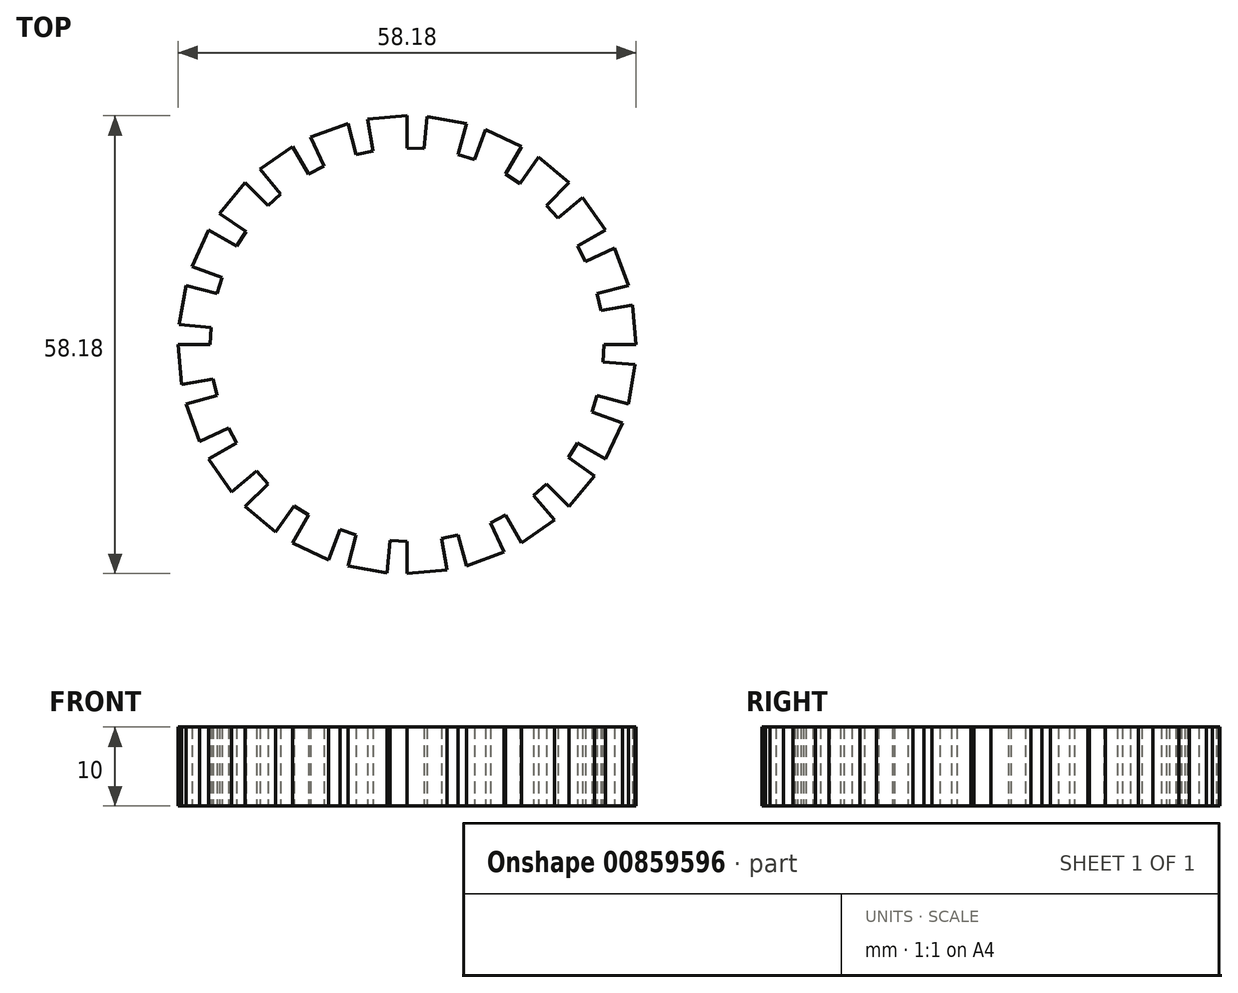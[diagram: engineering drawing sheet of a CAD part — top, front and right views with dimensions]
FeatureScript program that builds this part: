
annotation { "Feature Type Name" : "Feature", "Feature Type Description" : "" }
export const myFeature = defineFeature(function(context is Context, id is Id, definition is map)
    precondition{}
    {
        {
            var Q0;
            Q0=qCreatedBy(makeId("Top.planeOp"),FACE);
            var sketch = newSketch(context, id + "F0", { "sketchPlane" : qUnion([Q0])});
            skCircle(sketch, "E0", {"center": v(0, 0) * mm, "radius": 25 * mm, "construction": true});
            skLineSegment(sketch, "E1", {"start": v(0, 25) * mm, "end": v(0, 29.09) * mm});
            skCircle(sketch, "E2", {"center": v(0, 0) * mm, "radius": 29.09 * mm, "construction": true});
            skLineSegment(sketch, "E3", {"start": v(0, 0) * mm, "end": v(-5.05, 28.65) * mm, "construction": true});
            skLineSegment(sketch, "E4", {"start": v(0, 29.09) * mm, "end": v(-5.05, 28.65) * mm});
            skLineSegment(sketch, "E5", {"start": v(0, 0) * mm, "end": v(-7.53, 28.1) * mm, "construction": true});
            skLineSegment(sketch, "E6", {"start": v(-5.05, 28.65) * mm, "end": v(-4.34, 24.62) * mm});
            skLineSegment(sketch, "E7", {"start": v(-4.34, 24.62) * mm, "end": v(-6.47, 24.15) * mm});
            skLineSegment(sketch, "E8.1.0", {"start": v(-6.47, 24.15) * mm, "end": v(-7.53, 28.1) * mm});
            skLineSegment(sketch, "E8.1.1", {"start": v(-12.3, 26.36) * mm, "end": v(-10.57, 22.66) * mm});
            skLineSegment(sketch, "E8.1.2", {"start": v(-10.57, 22.66) * mm, "end": v(-12.5, 21.65) * mm});
            skLineSegment(sketch, "E8.1.3", {"start": v(-7.53, 28.1) * mm, "end": v(-12.3, 26.36) * mm});
            skLineSegment(sketch, "E8.2.0", {"start": v(-12.5, 21.65) * mm, "end": v(-14.54, 25.2) * mm});
            skLineSegment(sketch, "E8.2.1", {"start": v(-18.7, 22.28) * mm, "end": v(-16.07, 19.15) * mm});
            skLineSegment(sketch, "E8.2.2", {"start": v(-16.07, 19.15) * mm, "end": v(-17.68, 17.68) * mm});
            skLineSegment(sketch, "E8.2.3", {"start": v(-14.54, 25.2) * mm, "end": v(-18.7, 22.28) * mm});
            skLineSegment(sketch, "E8.3.0", {"start": v(-17.68, 17.68) * mm, "end": v(-20.57, 20.57) * mm});
            skLineSegment(sketch, "E8.3.1", {"start": v(-23.83, 16.68) * mm, "end": v(-20.48, 14.34) * mm});
            skLineSegment(sketch, "E8.3.2", {"start": v(-20.48, 14.34) * mm, "end": v(-21.65, 12.5) * mm});
            skLineSegment(sketch, "E8.3.3", {"start": v(-20.57, 20.57) * mm, "end": v(-23.83, 16.68) * mm});
            skLineSegment(sketch, "E8.4.0", {"start": v(-21.65, 12.5) * mm, "end": v(-25.2, 14.54) * mm});
            skLineSegment(sketch, "E8.4.1", {"start": v(-27.33, 9.95) * mm, "end": v(-23.5, 8.55) * mm});
            skLineSegment(sketch, "E8.4.2", {"start": v(-23.5, 8.55) * mm, "end": v(-24.15, 6.47) * mm});
            skLineSegment(sketch, "E8.4.3", {"start": v(-25.2, 14.54) * mm, "end": v(-27.33, 9.95) * mm});
            skLineSegment(sketch, "E8.5.0", {"start": v(-24.15, 6.47) * mm, "end": v(-28.1, 7.53) * mm});
            skLineSegment(sketch, "E8.5.1", {"start": v(-28.98, 2.54) * mm, "end": v(-24.9, 2.18) * mm});
            skLineSegment(sketch, "E8.5.2", {"start": v(-24.9, 2.18) * mm, "end": v(-25, 0) * mm});
            skLineSegment(sketch, "E8.5.3", {"start": v(-28.1, 7.53) * mm, "end": v(-28.98, 2.54) * mm});
            skLineSegment(sketch, "E8.6.0", {"start": v(-25, 0) * mm, "end": v(-29.09, 0) * mm});
            skLineSegment(sketch, "E8.6.1", {"start": v(-28.65, -5.05) * mm, "end": v(-24.62, -4.34) * mm});
            skLineSegment(sketch, "E8.6.2", {"start": v(-24.62, -4.34) * mm, "end": v(-24.15, -6.47) * mm});
            skLineSegment(sketch, "E8.6.3", {"start": v(-29.09, 0) * mm, "end": v(-28.65, -5.05) * mm});
            skLineSegment(sketch, "E8.7.0", {"start": v(-24.15, -6.47) * mm, "end": v(-28.1, -7.53) * mm});
            skLineSegment(sketch, "E8.7.1", {"start": v(-26.36, -12.3) * mm, "end": v(-22.66, -10.57) * mm});
            skLineSegment(sketch, "E8.7.2", {"start": v(-22.66, -10.57) * mm, "end": v(-21.65, -12.5) * mm});
            skLineSegment(sketch, "E8.7.3", {"start": v(-28.1, -7.53) * mm, "end": v(-26.36, -12.3) * mm});
            skLineSegment(sketch, "E8.8.0", {"start": v(-21.65, -12.5) * mm, "end": v(-25.2, -14.54) * mm});
            skLineSegment(sketch, "E8.8.1", {"start": v(-22.28, -18.7) * mm, "end": v(-19.15, -16.07) * mm});
            skLineSegment(sketch, "E8.8.2", {"start": v(-19.15, -16.07) * mm, "end": v(-17.68, -17.68) * mm});
            skLineSegment(sketch, "E8.8.3", {"start": v(-25.2, -14.54) * mm, "end": v(-22.28, -18.7) * mm});
            skLineSegment(sketch, "E8.9.0", {"start": v(-17.68, -17.68) * mm, "end": v(-20.57, -20.57) * mm});
            skLineSegment(sketch, "E8.9.1", {"start": v(-16.68, -23.83) * mm, "end": v(-14.34, -20.48) * mm});
            skLineSegment(sketch, "E8.9.2", {"start": v(-14.34, -20.48) * mm, "end": v(-12.5, -21.65) * mm});
            skLineSegment(sketch, "E8.9.3", {"start": v(-20.57, -20.57) * mm, "end": v(-16.68, -23.83) * mm});
            skLineSegment(sketch, "E8.10.0", {"start": v(-12.5, -21.65) * mm, "end": v(-14.54, -25.2) * mm});
            skLineSegment(sketch, "E8.10.1", {"start": v(-9.95, -27.33) * mm, "end": v(-8.55, -23.5) * mm});
            skLineSegment(sketch, "E8.10.2", {"start": v(-8.55, -23.5) * mm, "end": v(-6.47, -24.15) * mm});
            skLineSegment(sketch, "E8.10.3", {"start": v(-14.54, -25.2) * mm, "end": v(-9.95, -27.33) * mm});
            skLineSegment(sketch, "E8.11.0", {"start": v(-6.47, -24.15) * mm, "end": v(-7.53, -28.1) * mm});
            skLineSegment(sketch, "E8.11.1", {"start": v(-2.54, -28.98) * mm, "end": v(-2.18, -24.9) * mm});
            skLineSegment(sketch, "E8.11.2", {"start": v(-2.18, -24.9) * mm, "end": v(0, -25) * mm});
            skLineSegment(sketch, "E8.11.3", {"start": v(-7.53, -28.1) * mm, "end": v(-2.54, -28.98) * mm});
            skLineSegment(sketch, "E8.12.0", {"start": v(0, -25) * mm, "end": v(0, -29.09) * mm});
            skLineSegment(sketch, "E8.12.1", {"start": v(5.05, -28.65) * mm, "end": v(4.34, -24.62) * mm});
            skLineSegment(sketch, "E8.12.2", {"start": v(4.34, -24.62) * mm, "end": v(6.47, -24.15) * mm});
            skLineSegment(sketch, "E8.12.3", {"start": v(0, -29.09) * mm, "end": v(5.05, -28.65) * mm});
            skLineSegment(sketch, "E8.13.0", {"start": v(6.47, -24.15) * mm, "end": v(7.53, -28.1) * mm});
            skLineSegment(sketch, "E8.13.1", {"start": v(12.3, -26.36) * mm, "end": v(10.57, -22.66) * mm});
            skLineSegment(sketch, "E8.13.2", {"start": v(10.57, -22.66) * mm, "end": v(12.5, -21.65) * mm});
            skLineSegment(sketch, "E8.13.3", {"start": v(7.53, -28.1) * mm, "end": v(12.3, -26.36) * mm});
            skLineSegment(sketch, "E8.14.0", {"start": v(12.5, -21.65) * mm, "end": v(14.54, -25.2) * mm});
            skLineSegment(sketch, "E8.14.1", {"start": v(18.7, -22.28) * mm, "end": v(16.07, -19.15) * mm});
            skLineSegment(sketch, "E8.14.2", {"start": v(16.07, -19.15) * mm, "end": v(17.68, -17.68) * mm});
            skLineSegment(sketch, "E8.14.3", {"start": v(14.54, -25.2) * mm, "end": v(18.7, -22.28) * mm});
            skLineSegment(sketch, "E8.15.0", {"start": v(17.68, -17.68) * mm, "end": v(20.57, -20.57) * mm});
            skLineSegment(sketch, "E8.15.1", {"start": v(23.83, -16.68) * mm, "end": v(20.48, -14.34) * mm});
            skLineSegment(sketch, "E8.15.2", {"start": v(20.48, -14.34) * mm, "end": v(21.65, -12.5) * mm});
            skLineSegment(sketch, "E8.15.3", {"start": v(20.57, -20.57) * mm, "end": v(23.83, -16.68) * mm});
            skLineSegment(sketch, "E8.16.0", {"start": v(21.65, -12.5) * mm, "end": v(25.2, -14.54) * mm});
            skLineSegment(sketch, "E8.16.1", {"start": v(27.33, -9.95) * mm, "end": v(23.5, -8.55) * mm});
            skLineSegment(sketch, "E8.16.2", {"start": v(23.5, -8.55) * mm, "end": v(24.15, -6.47) * mm});
            skLineSegment(sketch, "E8.16.3", {"start": v(25.2, -14.54) * mm, "end": v(27.33, -9.95) * mm});
            skLineSegment(sketch, "E8.17.0", {"start": v(24.15, -6.47) * mm, "end": v(28.1, -7.53) * mm});
            skLineSegment(sketch, "E8.17.1", {"start": v(28.98, -2.54) * mm, "end": v(24.9, -2.18) * mm});
            skLineSegment(sketch, "E8.17.2", {"start": v(24.9, -2.18) * mm, "end": v(25, 0) * mm});
            skLineSegment(sketch, "E8.17.3", {"start": v(28.1, -7.53) * mm, "end": v(28.98, -2.54) * mm});
            skLineSegment(sketch, "E9.1.18.0", {"start": v(25, 0) * mm, "end": v(29.09, 0) * mm});
            skLineSegment(sketch, "E9.3.18.0", {"start": v(28.65, 5.05) * mm, "end": v(24.62, 4.34) * mm});
            skLineSegment(sketch, "E9.6.18.0", {"start": v(24.62, 4.34) * mm, "end": v(24.15, 6.47) * mm});
            skLineSegment(sketch, "E9.9.18.0", {"start": v(29.09, 0) * mm, "end": v(28.65, 5.05) * mm});
            skLineSegment(sketch, "E9.1.19.0", {"start": v(24.15, 6.47) * mm, "end": v(28.1, 7.53) * mm});
            skLineSegment(sketch, "E9.3.19.0", {"start": v(26.36, 12.3) * mm, "end": v(22.66, 10.57) * mm});
            skLineSegment(sketch, "E9.6.19.0", {"start": v(22.66, 10.57) * mm, "end": v(21.65, 12.5) * mm});
            skLineSegment(sketch, "E9.9.19.0", {"start": v(28.1, 7.53) * mm, "end": v(26.36, 12.3) * mm});
            skLineSegment(sketch, "E9.1.20.0", {"start": v(21.65, 12.5) * mm, "end": v(25.2, 14.54) * mm});
            skLineSegment(sketch, "E9.3.20.0", {"start": v(22.28, 18.7) * mm, "end": v(19.15, 16.07) * mm});
            skLineSegment(sketch, "E9.6.20.0", {"start": v(19.15, 16.07) * mm, "end": v(17.68, 17.68) * mm});
            skLineSegment(sketch, "E9.9.20.0", {"start": v(25.2, 14.54) * mm, "end": v(22.28, 18.7) * mm});
            skLineSegment(sketch, "E9.1.21.0", {"start": v(17.68, 17.68) * mm, "end": v(20.57, 20.57) * mm});
            skLineSegment(sketch, "E9.3.21.0", {"start": v(16.68, 23.83) * mm, "end": v(14.34, 20.48) * mm});
            skLineSegment(sketch, "E9.6.21.0", {"start": v(14.34, 20.48) * mm, "end": v(12.5, 21.65) * mm});
            skLineSegment(sketch, "E9.9.21.0", {"start": v(20.57, 20.57) * mm, "end": v(16.68, 23.83) * mm});
            skLineSegment(sketch, "E9.1.22.0", {"start": v(12.5, 21.65) * mm, "end": v(14.54, 25.2) * mm});
            skLineSegment(sketch, "E9.3.22.0", {"start": v(9.95, 27.33) * mm, "end": v(8.55, 23.5) * mm});
            skLineSegment(sketch, "E9.6.22.0", {"start": v(8.55, 23.5) * mm, "end": v(6.47, 24.15) * mm});
            skLineSegment(sketch, "E9.9.22.0", {"start": v(14.54, 25.2) * mm, "end": v(9.95, 27.33) * mm});
            skLineSegment(sketch, "E9.1.23.0", {"start": v(6.47, 24.15) * mm, "end": v(7.53, 28.1) * mm});
            skLineSegment(sketch, "E9.3.23.0", {"start": v(2.54, 28.98) * mm, "end": v(2.18, 24.9) * mm});
            skLineSegment(sketch, "E9.6.23.0", {"start": v(2.18, 24.9) * mm, "end": v(0, 25) * mm});
            skLineSegment(sketch, "E9.9.23.0", {"start": v(7.53, 28.1) * mm, "end": v(2.54, 28.98) * mm});
            skSolve(sketch);
        }
        {
            var Q0;
            Q0 = qSketchRegion(id + "F0", true);
            extrude(context, id + "F1", {"entities" : qUnion([Q0]), "depth" : 10 * mm, "offsetDistance" : 25 * mm});
        }
    });
